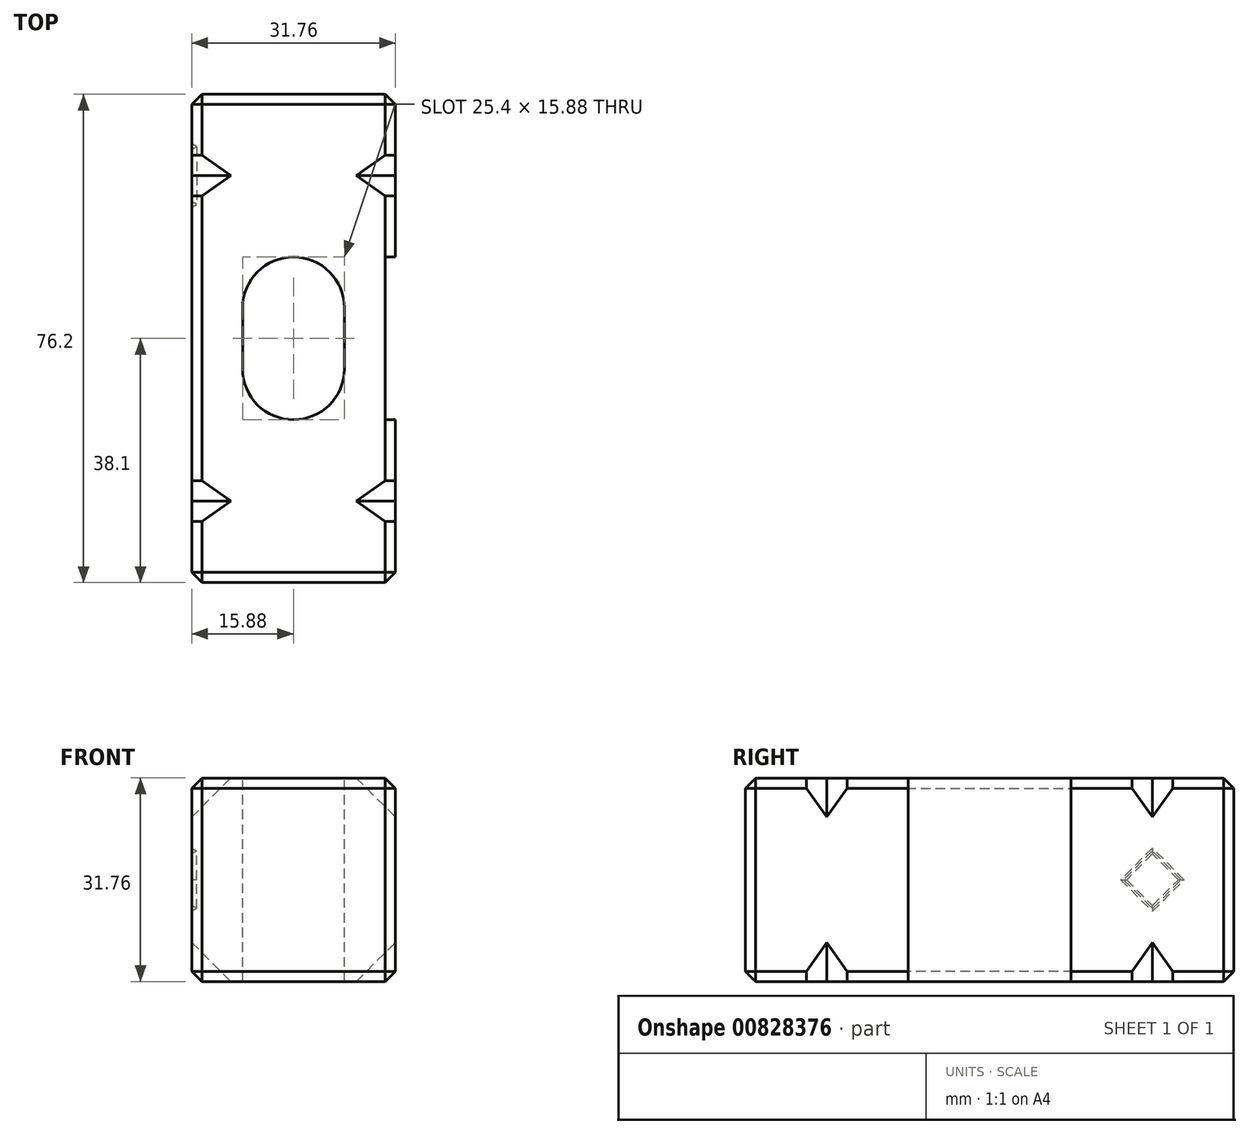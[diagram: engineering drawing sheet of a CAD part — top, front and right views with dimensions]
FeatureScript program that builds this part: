
annotation { "Feature Type Name" : "Feature", "Feature Type Description" : "" }
export const myFeature = defineFeature(function(context is Context, id is Id, definition is map)
    precondition{}
    {
        {
            var Q0;
            Q0=qCreatedBy(makeId("Front.planeOp"),FACE);
            var sketch = newSketch(context, id + "F0", { "sketchPlane" : qUnion([Q0])});
            skLineSegment(sketch, "E0", {"start": v(0, 15.88) * mm, "end": v(0, -15.88) * mm, "construction": true});
            skLineSegment(sketch, "E1", {"start": v(0, -15.88) * mm, "end": v(-15.87, 0) * mm, "construction": true});
            skLineSegment(sketch, "E2", {"start": v(-15.87, 0) * mm, "end": v(15.88, 0) * mm, "construction": true});
            skLineSegment(sketch, "E3.bottom", {"start": v(15.88, -15.88) * mm, "end": v(-15.87, -15.88) * mm});
            skLineSegment(sketch, "E3.top", {"start": v(15.88, 15.88) * mm, "end": v(-15.87, 15.88) * mm});
            skLineSegment(sketch, "E3.left", {"start": v(15.88, -15.88) * mm, "end": v(15.88, 15.88) * mm});
            skLineSegment(sketch, "E3.right", {"start": v(-15.87, -15.88) * mm, "end": v(-15.87, 15.88) * mm});
            skSolve(sketch);
        }
        {
            var Q0;
            Q0=makeQuery(id+"F0.imprint","IMPRINT",FACE,{"disambiguationData":[TD([[makeQuery(id+"F0.imprint","IMPRINT",EDGE,{"derivedFrom":sQuery(id+"F0.wireOp",EDGE,"E3.bottom")}),-1.0]])]});
            extrude(context, id + "F1", {"entities" : qUnion([Q0]), "endBound" : BoundingType.SYMMETRIC, "depth" : 76.2 * mm, "offsetDistance" : 25 * mm});
        }
        {
            var Q0;
            Q0=makeQuery(id+"F1.opExtrude","CAP_EDGE",EDGE,{"disambiguationData":[OSD([sQuery(id+"F0.wireOp",EDGE,"E3.top")])],"isStart":false});
            var Q1;
            Q1=makeQuery(id+"F1.opExtrude","CAP_EDGE",EDGE,{"disambiguationData":[OSD([sQuery(id+"F0.wireOp",EDGE,"E3.left")])],"isStart":false});
            var Q2;
            Q2=makeQuery(id+"F1.opExtrude","SWEPT_EDGE",EDGE,{"disambiguationData":[OSD([sQuery(id+"F0.wireOp",EDGE,"E3.top"),sQuery(id+"F0.wireOp",EDGE,"E3.left")])]});
            var Q3;
            Q3=makeQuery(id+"F1.opExtrude","SWEPT_EDGE",EDGE,{"disambiguationData":[OSD([sQuery(id+"F0.wireOp",EDGE,"E3.bottom"),sQuery(id+"F0.wireOp",EDGE,"E3.left")])]});
            var Q4;
            Q4=makeQuery(id+"F1.opExtrude","SWEPT_EDGE",EDGE,{"disambiguationData":[OSD([sQuery(id+"F0.wireOp",EDGE,"E3.top"),sQuery(id+"F0.wireOp",EDGE,"E3.right")])]});
            var Q5;
            Q5=makeQuery(id+"F1.opExtrude","CAP_EDGE",EDGE,{"disambiguationData":[OSD([sQuery(id+"F0.wireOp",EDGE,"E3.right")])],"isStart":false});
            var Q6;
            Q6=makeQuery(id+"F1.opExtrude","CAP_EDGE",EDGE,{"disambiguationData":[OSD([sQuery(id+"F0.wireOp",EDGE,"E3.bottom")])],"isStart":false});
            var Q7;
            Q7=makeQuery(id+"F1.opExtrude","CAP_EDGE",EDGE,{"disambiguationData":[OSD([sQuery(id+"F0.wireOp",EDGE,"E3.left")])],"isStart":true});
            var Q8;
            Q8=makeQuery(id+"F1.opExtrude","CAP_EDGE",EDGE,{"disambiguationData":[OSD([sQuery(id+"F0.wireOp",EDGE,"E3.right")])],"isStart":true});
            var Q9;
            Q9=makeQuery(id+"F1.opExtrude","CAP_EDGE",EDGE,{"disambiguationData":[OSD([sQuery(id+"F0.wireOp",EDGE,"E3.bottom")])],"isStart":true});
            var Q10;
            Q10=makeQuery(id+"F1.opExtrude","SWEPT_EDGE",EDGE,{"disambiguationData":[OSD([sQuery(id+"F0.wireOp",EDGE,"E3.bottom"),sQuery(id+"F0.wireOp",EDGE,"E3.right")])]});
            var Q11;
            Q11=makeQuery(id+"F1.opExtrude","CAP_EDGE",EDGE,{"disambiguationData":[OSD([sQuery(id+"F0.wireOp",EDGE,"E3.top")])],"isStart":true});
            chamfer(context, id + "F2", {"entities" : qUnion([Q0, Q1, Q2, Q3, Q4, Q5, Q6, Q7, Q8, Q9, Q10, Q11]), "width" : 1.59 * mm, "tangentPropagation" : true});
        }
        {
            var Q0;
            Q0=makeQuery(id+"F1.opExtrude","SWEPT_FACE",FACE,{"disambiguationData":[OSD([sQuery(id+"F0.wireOp",EDGE,"E3.top")])]});
            var sketch = newSketch(context, id + "F3", { "sketchPlane" : qUnion([Q0])});
            skLineSegment(sketch, "E4.0.0", {"start": v(14.29, -36.51) * mm, "end": v(14.29, 36.51) * mm});
            skLineSegment(sketch, "E4.0.1", {"start": v(14.29, 36.51) * mm, "end": v(-14.29, 36.51) * mm});
            skLineSegment(sketch, "E4.0.2", {"start": v(-14.29, 36.51) * mm, "end": v(-14.29, -36.51) * mm});
            skLineSegment(sketch, "E4.0.3", {"start": v(-14.29, -36.51) * mm, "end": v(14.29, -36.51) * mm});
            skLineSegment(sketch, "E5.0.0", {"start": v(-15.87, -36.51) * mm, "end": v(-14.29, -36.51) * mm});
            skLineSegment(sketch, "E5.0.1", {"start": v(-14.29, -36.51) * mm, "end": v(-14.29, 36.51) * mm});
            skLineSegment(sketch, "E5.0.2", {"start": v(-14.29, 36.51) * mm, "end": v(-15.87, 36.51) * mm});
            skLineSegment(sketch, "E5.0.3", {"start": v(-15.87, 36.51) * mm, "end": v(-15.87, -36.51) * mm});
            skLineSegment(sketch, "E6.0.0", {"start": v(14.29, -36.51) * mm, "end": v(15.88, -36.51) * mm});
            skLineSegment(sketch, "E6.0.1", {"start": v(15.88, -36.51) * mm, "end": v(15.88, 36.51) * mm});
            skLineSegment(sketch, "E6.0.2", {"start": v(14.29, 36.51) * mm, "end": v(15.88, 36.51) * mm});
            skLineSegment(sketch, "E6.0.3", {"start": v(14.29, 36.51) * mm, "end": v(14.29, -36.51) * mm});
            skLineSegment(sketch, "E7", {"start": v(-15.87, 0) * mm, "end": v(15.88, 0) * mm, "construction": true});
            skLineSegment(sketch, "E8", {"start": v(15.87, 12.7) * mm, "end": v(-15.87, 12.7) * mm, "construction": true});
            skLineSegment(sketch, "E9", {"start": v(-15.87, -12.7) * mm, "end": v(15.88, -12.7) * mm, "construction": true});
            skLineSegment(sketch, "E10", {"start": v(11.11, 36.51) * mm, "end": v(11.11, -36.51) * mm, "construction": true});
            skLineSegment(sketch, "E11", {"start": v(-11.11, 36.51) * mm, "end": v(-11.11, -36.51) * mm, "construction": true});
            skLineSegment(sketch, "E12", {"start": v(0, 36.51) * mm, "end": v(0, -36.51) * mm, "construction": true});
            skLineSegment(sketch, "E13", {"start": v(-14.29, 36.51) * mm, "end": v(-14.29, -36.51) * mm, "construction": true});
            skArc(sketch, "E14", {"start": v(-11.11, 12.7) * mm, "mid": v(-14.29, 0) * mm, "end": v(-11.11, -12.7) * mm});
            skLineSegment(sketch, "E15", {"start": v(-11.11, 12.7) * mm, "end": v(-15.87, 12.7) * mm});
            skLineSegment(sketch, "E16", {"start": v(-11.11, -12.7) * mm, "end": v(-15.87, -12.7) * mm});
            skLineSegment(sketch, "E17.MirrorCS", {"start": v(11.11, 12.7) * mm, "end": v(15.88, 12.7) * mm});
            skArc(sketch, "E18.MirrorCS", {"start": v(11.11, 12.7) * mm, "mid": v(14.29, 0) * mm, "end": v(11.11, -12.7) * mm});
            skLineSegment(sketch, "E19.MirrorCS", {"start": v(11.11, -12.7) * mm, "end": v(15.88, -12.7) * mm});
            skArc(sketch, "E20", {"start": v(-7.94, -4.76) * mm, "mid": v(0, -12.7) * mm, "end": v(7.94, -4.76) * mm});
            skLineSegment(sketch, "E21", {"start": v(7.94, 4.76) * mm, "end": v(7.94, -4.76) * mm});
            skLineSegment(sketch, "E22", {"start": v(-7.94, 4.76) * mm, "end": v(-7.94, -4.76) * mm});
            skArc(sketch, "E23.trimOffspring", {"start": v(7.94, 4.76) * mm, "mid": v(0, 12.7) * mm, "end": v(-7.94, 4.76) * mm});
            skSolve(sketch);
        }
        {
            var Q0;
            {var subQ0=sQuery(id+"F3.wireOp",EDGE,"E15");var subQ1=sQuery(id+"F3.wireOp",EDGE,"E5.0.1");var subQ2=makeQuery(id+"F3.imprint","INTERSECT",VERTEX,{"derivedFrom":[subQ1,subQ0]});Q0=makeQuery(id+"F3.imprint","IMPRINT",FACE,{"disambiguationData":[TD([[makeQuery(id+"F3.imprint","IMPRINT",EDGE,{"disambiguationData":[TD([[subQ2,-1.0]])],"derivedFrom":subQ1}),1.0]])]});}
            var Q1;
            {var subQ1=sQuery(id+"F3.wireOp",EDGE,"E5.0.1");var subQ4=sQuery(id+"F3.wireOp",EDGE,"E15");var subQ10=makeQuery(id+"F3.imprint","INTERSECT",VERTEX,{"derivedFrom":[subQ1,subQ4]});Q1=makeQuery(id+"F3.imprint","IMPRINT",FACE,{"disambiguationData":[TD([[makeQuery(id+"F3.imprint","IMPRINT",EDGE,{"disambiguationData":[TD([[subQ10,-1.0]])],"derivedFrom":subQ1}),-1.0]])]});}
            var Q2;
            {var subQ0=sQuery(id+"F3.wireOp",EDGE,"E14");var subQ1=sQuery(id+"F3.wireOp",EDGE,"E5.0.1");var subQ2=makeQuery(id+"F3.imprint","INTERSECT",VERTEX,{"disambiguationData":[OD(1.0)],"derivedFrom":[subQ1,subQ0]});Q2=makeQuery(id+"F3.imprint","IMPRINT",FACE,{"disambiguationData":[TD([[makeQuery(id+"F3.imprint","IMPRINT",EDGE,{"disambiguationData":[TD([[subQ2,-1.0]])],"derivedFrom":subQ1}),1.0]])]});}
            var Q3;
            {var subQ0=sQuery(id+"F3.wireOp",EDGE,"E19.MirrorCS");var subQ1=sQuery(id+"F3.wireOp",EDGE,"E6.0.3");var subQ2=makeQuery(id+"F3.imprint","INTERSECT",VERTEX,{"derivedFrom":[subQ1,subQ0]});Q3=makeQuery(id+"F3.imprint","IMPRINT",FACE,{"disambiguationData":[TD([[makeQuery(id+"F3.imprint","IMPRINT",EDGE,{"disambiguationData":[TD([[subQ2,-1.0]])],"derivedFrom":subQ1}),1.0]])]});}
            var Q4;
            {var subQ0=sQuery(id+"F3.wireOp",EDGE,"E17.MirrorCS");var subQ1=sQuery(id+"F3.wireOp",EDGE,"E6.0.1");var subQ2=makeQuery(id+"F3.imprint","INTERSECT",VERTEX,{"derivedFrom":[subQ1,subQ0]});Q4=makeQuery(id+"F3.imprint","IMPRINT",FACE,{"disambiguationData":[TD([[makeQuery(id+"F3.imprint","IMPRINT",EDGE,{"disambiguationData":[TD([[subQ2,1.0]])],"derivedFrom":subQ1}),1.0]])]});}
            var Q5;
            {var subQ0=sQuery(id+"F3.wireOp",EDGE,"E18.MirrorCS");var subQ1=sQuery(id+"F3.wireOp",EDGE,"E6.0.3");var subQ2=makeQuery(id+"F3.imprint","INTERSECT",VERTEX,{"disambiguationData":[OD(1.0)],"derivedFrom":[subQ1,subQ0]});Q5=makeQuery(id+"F3.imprint","IMPRINT",FACE,{"disambiguationData":[TD([[makeQuery(id+"F3.imprint","IMPRINT",EDGE,{"disambiguationData":[TD([[subQ2,-1.0]])],"derivedFrom":subQ1}),1.0]])]});}
            var Q6;
            Q6=makeQuery(id+"F3.imprint","IMPRINT",FACE,{"disambiguationData":[TD([[makeQuery(id+"F3.imprint","IMPRINT",EDGE,{"derivedFrom":sQuery(id+"F3.wireOp",EDGE,"E20")}),1.0]])]});
            extrude(context, id + "F4", {"entities" : qUnion([Q0, Q1, Q2, Q3, Q4, Q5, Q6]), "operationType" : NewBodyOperationType.REMOVE, "endBound" : BoundingType.THROUGH_ALL, "oppositeDirection" : true, "depth" : 25.4 * mm, "offsetDistance" : 25.4 * mm});
        }
        {
            var Q0;
            {var subQ0=sQuery(id+"F0.wireOp",EDGE,"E3.right");var subQ1=sQuery(id+"F0.wireOp",EDGE,"E3.top");Q0=makeQuery(id+"F2.opChamfer","BLEND_VERTEX",VERTEX,{"blendedFrom":[makeQuery(id+"F1.opExtrude","CAP_VERTEX",VERTEX,{"disambiguationData":[OSD([subQ1,subQ0])],"isStart":true}),makeQuery(id+"F1.opExtrude","CAP_EDGE",EDGE,{"disambiguationData":[OSD([subQ1])],"isStart":true}),makeQuery(id+"F1.opExtrude","CAP_EDGE",EDGE,{"disambiguationData":[OSD([subQ0])],"isStart":true}),makeQuery(id+"F1.opExtrude","CAP_FACE",FACE,{"disambiguationData":[OSD([sQuery(id+"F0.wireOp",EDGE,"E3.bottom"),subQ1,sQuery(id+"F0.wireOp",EDGE,"E3.left"),subQ0])],"isStart":true})],"blendedInto":[makeQuery(id+"F1.opExtrude","CAP_FACE",FACE,{"disambiguationData":[OSD([sQuery(id+"F0.wireOp",EDGE,"E3.bottom"),subQ1,sQuery(id+"F0.wireOp",EDGE,"E3.left"),subQ0])],"isStart":true})]});}
            var Q1;
            {var subQ0=sQuery(id+"F0.wireOp",EDGE,"E3.left");var subQ1=sQuery(id+"F0.wireOp",EDGE,"E3.bottom");Q1=makeQuery(id+"F2.opChamfer","BLEND_VERTEX",VERTEX,{"blendedFrom":[makeQuery(id+"F1.opExtrude","CAP_VERTEX",VERTEX,{"disambiguationData":[OSD([subQ1,subQ0])],"isStart":true}),makeQuery(id+"F1.opExtrude","CAP_EDGE",EDGE,{"disambiguationData":[OSD([subQ1])],"isStart":true}),makeQuery(id+"F1.opExtrude","CAP_EDGE",EDGE,{"disambiguationData":[OSD([subQ0])],"isStart":true}),makeQuery(id+"F1.opExtrude","CAP_FACE",FACE,{"disambiguationData":[OSD([subQ1,sQuery(id+"F0.wireOp",EDGE,"E3.top"),subQ0,sQuery(id+"F0.wireOp",EDGE,"E3.right")])],"isStart":true})],"blendedInto":[makeQuery(id+"F1.opExtrude","CAP_FACE",FACE,{"disambiguationData":[OSD([subQ1,sQuery(id+"F0.wireOp",EDGE,"E3.top"),subQ0,sQuery(id+"F0.wireOp",EDGE,"E3.right")])],"isStart":true})]});}
            var Q2;
            {var subQ0=sQuery(id+"F0.wireOp",EDGE,"E3.left");var subQ1=sQuery(id+"F0.wireOp",EDGE,"E3.bottom");Q2=makeQuery(id+"F2.opChamfer","BLEND_VERTEX",VERTEX,{"blendedFrom":[makeQuery(id+"F1.opExtrude","CAP_VERTEX",VERTEX,{"disambiguationData":[OSD([subQ1,subQ0])],"isStart":false}),makeQuery(id+"F1.opExtrude","CAP_EDGE",EDGE,{"disambiguationData":[OSD([subQ1])],"isStart":false}),makeQuery(id+"F1.opExtrude","CAP_EDGE",EDGE,{"disambiguationData":[OSD([subQ0])],"isStart":false}),makeQuery(id+"F1.opExtrude","CAP_FACE",FACE,{"disambiguationData":[OSD([subQ1,sQuery(id+"F0.wireOp",EDGE,"E3.top"),subQ0,sQuery(id+"F0.wireOp",EDGE,"E3.right")])],"isStart":false})],"blendedInto":[makeQuery(id+"F1.opExtrude","CAP_FACE",FACE,{"disambiguationData":[OSD([subQ1,sQuery(id+"F0.wireOp",EDGE,"E3.top"),subQ0,sQuery(id+"F0.wireOp",EDGE,"E3.right")])],"isStart":false})]});}
            cPlane(context, id + "F5", {"entities" : qUnion([Q0, Q1, Q2]), "cplaneType" : CPlaneType.THREE_POINT, "offset" : 25.4 * mm, "width" : 152.4 * mm, "height" : 152.4 * mm});
        }
        {
            var Q0;
            Q0=qCreatedBy(id+"F5.planeOp",FACE);
            var sketch = newSketch(context, id + "F6", { "sketchPlane" : qUnion([Q0])});
            skEllipticalArc(sketch, "E24.0.0", {});
            skLineSegment(sketch, "E24.0.1", {"start": v(-12.7, 19.08) * mm, "end": v(-12.7, 21.33) * mm});
            skLineSegment(sketch, "E24.0.2", {"start": v(-12.7, 21.33) * mm, "end": v(-36.51, 21.33) * mm});
            skLineSegment(sketch, "E24.0.3", {"start": v(-36.51, 21.33) * mm, "end": v(-36.51, 1.12) * mm});
            skLineSegment(sketch, "E24.0.4", {"start": v(-36.51, 1.12) * mm, "end": v(-12.7, 1.12) * mm});
            skLineSegment(sketch, "E24.0.5", {"start": v(-12.7, 1.12) * mm, "end": v(-12.7, 3.37) * mm});
            skEllipticalArc(sketch, "E24.0.6", {});
            skLineSegment(sketch, "E24.0.7", {"start": v(12.7, 3.37) * mm, "end": v(12.7, 1.12) * mm});
            skLineSegment(sketch, "E24.0.8", {"start": v(12.7, 1.12) * mm, "end": v(36.51, 1.12) * mm});
            skLineSegment(sketch, "E24.0.9", {"start": v(36.51, 1.12) * mm, "end": v(36.51, 21.33) * mm});
            skLineSegment(sketch, "E24.0.10", {"start": v(36.51, 21.33) * mm, "end": v(12.7, 21.33) * mm});
            skLineSegment(sketch, "E24.0.11", {"start": v(12.7, 21.33) * mm, "end": v(12.7, 19.08) * mm});
            skLineSegment(sketch, "E25.0.0", {"start": v(-38.1, 20.2) * mm, "end": v(-38.1, 0) * mm});
            skLineSegment(sketch, "E25.0.1", {"start": v(-38.1, 0) * mm, "end": v(-38.1, -20.2) * mm});
            skLineSegment(sketch, "E25.0.2", {"start": v(-38.1, -20.2) * mm, "end": v(-38.1, 0) * mm});
            skLineSegment(sketch, "E25.0.3", {"start": v(-38.1, 0) * mm, "end": v(-38.1, 20.2) * mm});
            skLineSegment(sketch, "E26.0.0", {"start": v(-36.51, -21.33) * mm, "end": v(-12.7, -21.33) * mm});
            skLineSegment(sketch, "E26.0.1", {"start": v(-12.7, -21.33) * mm, "end": v(-12.7, -1.12) * mm});
            skLineSegment(sketch, "E26.0.2", {"start": v(-12.7, -1.12) * mm, "end": v(-36.51, -1.12) * mm});
            skLineSegment(sketch, "E26.0.3", {"start": v(-36.51, -1.12) * mm, "end": v(-36.51, -21.33) * mm});
            skLineSegment(sketch, "E27.0.0", {"start": v(12.7, -1.12) * mm, "end": v(12.7, -21.33) * mm});
            skLineSegment(sketch, "E27.0.1", {"start": v(12.7, -21.33) * mm, "end": v(36.51, -21.33) * mm});
            skLineSegment(sketch, "E27.0.2", {"start": v(36.51, -21.33) * mm, "end": v(36.51, -1.12) * mm});
            skLineSegment(sketch, "E27.0.3", {"start": v(36.51, -1.12) * mm, "end": v(12.7, -1.12) * mm});
            skLineSegment(sketch, "E28.0.0", {"start": v(36.51, 1.12) * mm, "end": v(12.7, 1.12) * mm});
            skLineSegment(sketch, "E28.0.1", {"start": v(12.7, 1.12) * mm, "end": v(12.7, -1.12) * mm});
            skLineSegment(sketch, "E28.0.2", {"start": v(12.7, -1.12) * mm, "end": v(36.51, -1.12) * mm});
            skLineSegment(sketch, "E28.0.3", {"start": v(36.51, 1.12) * mm, "end": v(36.51, -1.12) * mm});
            skLineSegment(sketch, "E29.0.0", {"start": v(-12.7, 1.12) * mm, "end": v(-12.7, -1.12) * mm});
            skLineSegment(sketch, "E29.0.1", {"start": v(-12.7, 1.12) * mm, "end": v(-36.51, 1.12) * mm});
            skLineSegment(sketch, "E29.0.2", {"start": v(-36.51, 1.12) * mm, "end": v(-36.51, -1.12) * mm});
            skLineSegment(sketch, "E29.0.3", {"start": v(-36.51, -1.12) * mm, "end": v(-12.7, -1.12) * mm});
            skEllipticalArc(sketch, "E30.0.0", {});
            skLineSegment(sketch, "E30.0.1", {"start": v(12.7, -19.08) * mm, "end": v(12.7, 3.37) * mm});
            skEllipticalArc(sketch, "E30.0.2", {});
            skLineSegment(sketch, "E30.0.3", {"start": v(-12.7, 3.37) * mm, "end": v(-12.7, -19.08) * mm});
            skLineSegment(sketch, "E31.0.1", {"start": v(-12.7, -21.33) * mm, "end": v(-36.51, -21.33) * mm});
            skLineSegment(sketch, "E32.0.0", {"start": v(36.51, -21.33) * mm, "end": v(12.7, -21.33) * mm});
            skLineSegment(sketch, "E33.0.1", {"start": v(-12.7, -1.12) * mm, "end": v(-12.7, -3.37) * mm});
            skEllipticalArc(sketch, "E33.0.2", {});
            skLineSegment(sketch, "E33.0.3", {"start": v(12.7, -3.37) * mm, "end": v(12.7, -1.12) * mm});
            skLineSegment(sketch, "E33.0.5", {"start": v(36.51, -1.12) * mm, "end": v(36.51, -21.33) * mm});
            skLineSegment(sketch, "E33.0.7", {"start": v(12.7, -21.33) * mm, "end": v(12.7, -19.08) * mm});
            skEllipticalArc(sketch, "E33.0.8", {});
            skLineSegment(sketch, "E33.0.9", {"start": v(-12.7, -19.08) * mm, "end": v(-12.7, -21.33) * mm});
            skLineSegment(sketch, "E33.0.11", {"start": v(-36.51, -21.33) * mm, "end": v(-36.51, -1.12) * mm});
            skLineSegment(sketch, "E34.0.0", {"start": v(38.1, -20.2) * mm, "end": v(38.1, 0) * mm});
            skLineSegment(sketch, "E34.0.1", {"start": v(38.1, 0) * mm, "end": v(38.1, 20.2) * mm});
            skLineSegment(sketch, "E34.0.2", {"start": v(38.1, 20.2) * mm, "end": v(38.1, 0) * mm});
            skLineSegment(sketch, "E34.0.3", {"start": v(38.1, 0) * mm, "end": v(38.1, -20.2) * mm});
            skLineSegment(sketch, "E35", {"start": v(-25.4, 21.33) * mm, "end": v(-25.4, -21.33) * mm, "construction": true});
            skLineSegment(sketch, "E36", {"start": v(25.4, -21.33) * mm, "end": v(25.4, 21.33) * mm, "construction": true});
            skLineSegment(sketch, "E37", {"start": v(0, 38.1) * mm, "end": v(0, -38.1) * mm, "construction": true});
            skLineSegment(sketch, "E38", {"start": v(-25.4, 18.15) * mm, "end": v(-22.22, 21.33) * mm});
            skLineSegment(sketch, "E39", {"start": v(-22.22, 21.33) * mm, "end": v(-25.4, 18.15) * mm});
            skLineSegment(sketch, "E40", {"start": v(-25.4, 18.15) * mm, "end": v(-28.58, 21.33) * mm});
            skLineSegment(sketch, "E41", {"start": v(-38.1, 0) * mm, "end": v(38.1, 0) * mm, "construction": true});
            skLineSegment(sketch, "E42.MirrorCS", {"start": v(-25.4, -18.15) * mm, "end": v(-22.22, -21.33) * mm});
            skLineSegment(sketch, "E43.MirrorCS", {"start": v(-25.4, -18.15) * mm, "end": v(-28.58, -21.33) * mm});
            skLineSegment(sketch, "E44.MirrorCS", {"start": v(25.4, 18.15) * mm, "end": v(22.22, 21.33) * mm});
            skLineSegment(sketch, "E45.MirrorCS", {"start": v(25.4, 18.15) * mm, "end": v(28.58, 21.33) * mm});
            skLineSegment(sketch, "E46.MirrorCS", {"start": v(25.4, -18.15) * mm, "end": v(22.22, -21.33) * mm});
            skLineSegment(sketch, "E47.MirrorCS", {"start": v(25.4, -18.15) * mm, "end": v(28.58, -21.33) * mm});
            const initialGuessF6  = {"E24.0.0": [0, 0.002245064030267274, 1, 0, 0.02698750000000002, 0.01908304425727196, 1.0808390005411692, 2.060753653048625], "E24.0.6": [0, 0.020205576272405608, 1, 0, 0.02698750000000002, 0.01908304425727196, 4.222431654130961, 5.202346306638417], "E30.0.0": [0, -0.00224506403026728, 1, 0, 0.02698750000000002, 0.019083044257271958, 4.222431654130962, 5.202346306638416], "E30.0.2": [0, 0.020205576272405608, -1, 0, 0.02698750000000002, 0.01908304425727196, 1.0808390005411683, 2.0607536530486246], "E33.0.2": [0, -0.020205576272405615, -1, 0, 0.02698750000000002, 0.019083044257271958, 4.222431654130962, 5.202346306638418], "E33.0.8": [0, -0.00224506403026728, -1, 0, 0.02698750000000002, 0.019083044257271958, 1.0808390005411688, 2.0607536530486237]};
            skSetInitialGuess(sketch, initialGuessF6);
            skSolve(sketch);
        }
        {
            var Q0;
            {var subQ2=sQuery(id+"F6.wireOp",EDGE,"E38");Q0=makeQuery(id+"F6.imprint","IMPRINT",FACE,{"disambiguationData":[TD([[makeQuery(id+"F6.imprint","IMPRINT",EDGE,{"derivedFrom":subQ2}),1.0]])]});}
            var Q1;
            {var subQ0=sQuery(id+"F6.wireOp",EDGE,"E42.MirrorCS");Q1=makeQuery(id+"F6.imprint","IMPRINT",FACE,{"disambiguationData":[TD([[makeQuery(id+"F6.imprint","IMPRINT",EDGE,{"derivedFrom":subQ0}),-1.0]])]});}
            var Q2;
            {var subQ2=sQuery(id+"F6.wireOp",EDGE,"E46.MirrorCS");Q2=makeQuery(id+"F6.imprint","IMPRINT",FACE,{"disambiguationData":[TD([[makeQuery(id+"F6.imprint","IMPRINT",EDGE,{"derivedFrom":subQ2}),1.0]])]});}
            var Q3;
            {var subQ0=sQuery(id+"F6.wireOp",EDGE,"E44.MirrorCS");Q3=makeQuery(id+"F6.imprint","IMPRINT",FACE,{"disambiguationData":[TD([[makeQuery(id+"F6.imprint","IMPRINT",EDGE,{"derivedFrom":subQ0}),-1.0]])]});}
            extrude(context, id + "F7", {"entities" : qUnion([Q0, Q1, Q2, Q3]), "operationType" : NewBodyOperationType.REMOVE, "endBound" : BoundingType.SYMMETRIC, "oppositeDirection" : true, "depth" : 25.4 * mm, "offsetDistance" : 25.4 * mm});
        }
        {
            var Q0;
            {var subQ0=sQuery(id+"F0.wireOp",EDGE,"E3.left");var subQ1=sQuery(id+"F0.wireOp",EDGE,"E3.top");Q0=makeQuery(id+"F2.opChamfer","BLEND_VERTEX",VERTEX,{"blendedFrom":[makeQuery(id+"F1.opExtrude","CAP_VERTEX",VERTEX,{"disambiguationData":[OSD([subQ1,subQ0])],"isStart":true}),makeQuery(id+"F1.opExtrude","CAP_EDGE",EDGE,{"disambiguationData":[OSD([subQ1])],"isStart":true}),makeQuery(id+"F1.opExtrude","CAP_EDGE",EDGE,{"disambiguationData":[OSD([subQ0])],"isStart":true}),makeQuery(id+"F1.opExtrude","CAP_FACE",FACE,{"disambiguationData":[OSD([sQuery(id+"F0.wireOp",EDGE,"E3.bottom"),subQ1,subQ0,sQuery(id+"F0.wireOp",EDGE,"E3.right")])],"isStart":true})],"blendedInto":[makeQuery(id+"F1.opExtrude","CAP_FACE",FACE,{"disambiguationData":[OSD([sQuery(id+"F0.wireOp",EDGE,"E3.bottom"),subQ1,subQ0,sQuery(id+"F0.wireOp",EDGE,"E3.right")])],"isStart":true})]});}
            var Q1;
            {var subQ0=sQuery(id+"F0.wireOp",EDGE,"E3.right");var subQ1=sQuery(id+"F0.wireOp",EDGE,"E3.bottom");Q1=makeQuery(id+"F2.opChamfer","BLEND_VERTEX",VERTEX,{"blendedFrom":[makeQuery(id+"F1.opExtrude","CAP_VERTEX",VERTEX,{"disambiguationData":[OSD([subQ1,subQ0])],"isStart":true}),makeQuery(id+"F1.opExtrude","CAP_EDGE",EDGE,{"disambiguationData":[OSD([subQ1])],"isStart":true}),makeQuery(id+"F1.opExtrude","CAP_EDGE",EDGE,{"disambiguationData":[OSD([subQ0])],"isStart":true}),makeQuery(id+"F1.opExtrude","CAP_FACE",FACE,{"disambiguationData":[OSD([subQ1,sQuery(id+"F0.wireOp",EDGE,"E3.top"),sQuery(id+"F0.wireOp",EDGE,"E3.left"),subQ0])],"isStart":true})],"blendedInto":[makeQuery(id+"F1.opExtrude","CAP_FACE",FACE,{"disambiguationData":[OSD([subQ1,sQuery(id+"F0.wireOp",EDGE,"E3.top"),sQuery(id+"F0.wireOp",EDGE,"E3.left"),subQ0])],"isStart":true})]});}
            var Q2;
            {var subQ0=sQuery(id+"F0.wireOp",EDGE,"E3.left");var subQ1=sQuery(id+"F0.wireOp",EDGE,"E3.top");Q2=makeQuery(id+"F2.opChamfer","BLEND_VERTEX",VERTEX,{"blendedFrom":[makeQuery(id+"F1.opExtrude","CAP_VERTEX",VERTEX,{"disambiguationData":[OSD([subQ1,subQ0])],"isStart":false}),makeQuery(id+"F1.opExtrude","CAP_EDGE",EDGE,{"disambiguationData":[OSD([subQ1])],"isStart":false}),makeQuery(id+"F1.opExtrude","CAP_EDGE",EDGE,{"disambiguationData":[OSD([subQ0])],"isStart":false}),makeQuery(id+"F1.opExtrude","CAP_FACE",FACE,{"disambiguationData":[OSD([sQuery(id+"F0.wireOp",EDGE,"E3.bottom"),subQ1,subQ0,sQuery(id+"F0.wireOp",EDGE,"E3.right")])],"isStart":false})],"blendedInto":[makeQuery(id+"F1.opExtrude","CAP_FACE",FACE,{"disambiguationData":[OSD([sQuery(id+"F0.wireOp",EDGE,"E3.bottom"),subQ1,subQ0,sQuery(id+"F0.wireOp",EDGE,"E3.right")])],"isStart":false})]});}
            cPlane(context, id + "F8", {"entities" : qUnion([Q0, Q1, Q2]), "cplaneType" : CPlaneType.THREE_POINT, "offset" : 25.4 * mm, "width" : 152.4 * mm, "height" : 152.4 * mm});
        }
        {
            var Q0;
            Q0=qCreatedBy(id+"F8.planeOp",FACE);
            var sketch = newSketch(context, id + "F9", { "sketchPlane" : qUnion([Q0])});
            skLineSegment(sketch, "E48.0.0", {"start": v(12.7, -1.12) * mm, "end": v(22.22, -1.12) * mm});
            skLineSegment(sketch, "E48.0.1", {"start": v(22.23, -1.12) * mm, "end": v(25.4, -4.3) * mm});
            skLineSegment(sketch, "E48.0.2", {"start": v(25.4, -4.3) * mm, "end": v(28.57, -1.12) * mm});
            skLineSegment(sketch, "E48.0.3", {"start": v(28.57, -1.12) * mm, "end": v(36.51, -1.12) * mm});
            skLineSegment(sketch, "E48.0.4", {"start": v(36.51, -1.12) * mm, "end": v(36.51, -21.33) * mm});
            skLineSegment(sketch, "E48.0.5", {"start": v(36.51, -21.33) * mm, "end": v(12.7, -21.33) * mm});
            skLineSegment(sketch, "E48.0.6", {"start": v(12.7, -21.33) * mm, "end": v(12.7, -1.12) * mm});
            skLineSegment(sketch, "E49.0.0", {"start": v(-28.58, -1.12) * mm, "end": v(-25.4, -4.3) * mm});
            skLineSegment(sketch, "E49.0.1", {"start": v(-25.4, -4.3) * mm, "end": v(-22.23, -1.12) * mm});
            skLineSegment(sketch, "E49.0.2", {"start": v(-22.23, -1.12) * mm, "end": v(-12.7, -1.12) * mm});
            skLineSegment(sketch, "E49.0.3", {"start": v(-12.7, -1.12) * mm, "end": v(-12.7, -21.33) * mm});
            skLineSegment(sketch, "E49.0.4", {"start": v(-12.7, -21.33) * mm, "end": v(-36.51, -21.33) * mm});
            skLineSegment(sketch, "E49.0.5", {"start": v(-36.51, -21.33) * mm, "end": v(-36.51, -1.12) * mm});
            skLineSegment(sketch, "E49.0.6", {"start": v(-36.51, -1.12) * mm, "end": v(-28.58, -1.12) * mm});
            skLineSegment(sketch, "E50.0.1", {"start": v(-12.7, 21.33) * mm, "end": v(-36.51, 21.33) * mm});
            skLineSegment(sketch, "E50.0.3", {"start": v(-36.51, 21.33) * mm, "end": v(-12.7, 21.33) * mm});
            skLineSegment(sketch, "E51.0.0", {"start": v(36.51, 21.33) * mm, "end": v(12.7, 21.33) * mm});
            skLineSegment(sketch, "E51.0.2", {"start": v(12.7, 21.33) * mm, "end": v(36.51, 21.33) * mm});
            skLineSegment(sketch, "E52.0.0", {"start": v(-25.4, 4.3) * mm, "end": v(-22.22, 1.12) * mm});
            skLineSegment(sketch, "E52.0.1", {"start": v(-22.22, 1.12) * mm, "end": v(-12.7, 1.12) * mm});
            skLineSegment(sketch, "E52.0.2", {"start": v(-12.7, 1.12) * mm, "end": v(-12.7, 21.33) * mm});
            skLineSegment(sketch, "E52.0.4", {"start": v(-36.51, 21.33) * mm, "end": v(-36.51, 1.12) * mm});
            skLineSegment(sketch, "E52.0.5", {"start": v(-36.51, 1.12) * mm, "end": v(-28.58, 1.12) * mm});
            skLineSegment(sketch, "E52.0.6", {"start": v(-28.57, 1.12) * mm, "end": v(-25.4, 4.3) * mm});
            skLineSegment(sketch, "E53.0.0", {"start": v(25.4, 4.3) * mm, "end": v(28.58, 1.12) * mm});
            skLineSegment(sketch, "E53.0.1", {"start": v(28.58, 1.12) * mm, "end": v(36.51, 1.12) * mm});
            skLineSegment(sketch, "E53.0.2", {"start": v(36.51, 1.12) * mm, "end": v(36.51, 21.33) * mm});
            skLineSegment(sketch, "E53.0.4", {"start": v(12.7, 21.33) * mm, "end": v(12.7, 1.12) * mm});
            skLineSegment(sketch, "E53.0.5", {"start": v(12.7, 1.12) * mm, "end": v(22.22, 1.12) * mm});
            skLineSegment(sketch, "E53.0.6", {"start": v(22.23, 1.12) * mm, "end": v(25.4, 4.3) * mm});
            skLineSegment(sketch, "E54.0.0", {"start": v(36.51, -1.12) * mm, "end": v(28.58, -1.12) * mm});
            skLineSegment(sketch, "E54.0.1", {"start": v(28.58, -1.12) * mm, "end": v(25.4, -4.3) * mm});
            skLineSegment(sketch, "E54.0.2", {"start": v(25.4, -4.3) * mm, "end": v(22.23, -1.12) * mm});
            skLineSegment(sketch, "E54.0.3", {"start": v(22.23, -1.12) * mm, "end": v(12.7, -1.12) * mm});
            skLineSegment(sketch, "E54.0.4", {"start": v(12.7, -1.12) * mm, "end": v(12.7, -3.37) * mm});
            skEllipticalArc(sketch, "E54.0.5", {});
            skLineSegment(sketch, "E54.0.6", {"start": v(-12.7, -3.37) * mm, "end": v(-12.7, -1.12) * mm});
            skLineSegment(sketch, "E54.0.7", {"start": v(-12.7, -1.12) * mm, "end": v(-22.22, -1.12) * mm});
            skLineSegment(sketch, "E54.0.8", {"start": v(-22.22, -1.12) * mm, "end": v(-25.4, -4.3) * mm});
            skLineSegment(sketch, "E54.0.9", {"start": v(-25.4, -4.3) * mm, "end": v(-28.57, -1.12) * mm});
            skLineSegment(sketch, "E54.0.10", {"start": v(-28.57, -1.12) * mm, "end": v(-36.51, -1.12) * mm});
            skLineSegment(sketch, "E54.0.11", {"start": v(-36.51, -1.12) * mm, "end": v(-36.51, -21.33) * mm});
            skLineSegment(sketch, "E54.0.12", {"start": v(-36.51, -21.33) * mm, "end": v(-12.7, -21.33) * mm});
            skLineSegment(sketch, "E54.0.13", {"start": v(-12.7, -21.33) * mm, "end": v(-12.7, -19.08) * mm});
            skEllipticalArc(sketch, "E54.0.14", {});
            skLineSegment(sketch, "E54.0.15", {"start": v(12.7, -19.08) * mm, "end": v(12.7, -21.33) * mm});
            skLineSegment(sketch, "E54.0.16", {"start": v(12.7, -21.33) * mm, "end": v(36.51, -21.33) * mm});
            skLineSegment(sketch, "E54.0.17", {"start": v(36.51, -21.33) * mm, "end": v(36.51, -1.12) * mm});
            skLineSegment(sketch, "E55.0.0", {"start": v(25.4, 4.3) * mm, "end": v(22.23, 1.12) * mm});
            skLineSegment(sketch, "E55.0.1", {"start": v(22.23, 1.12) * mm, "end": v(12.7, 1.12) * mm});
            skLineSegment(sketch, "E55.0.2", {"start": v(12.7, 1.12) * mm, "end": v(12.7, 3.37) * mm});
            skEllipticalArc(sketch, "E55.0.3", {});
            skLineSegment(sketch, "E55.0.4", {"start": v(-12.7, 3.37) * mm, "end": v(-12.7, 1.12) * mm});
            skLineSegment(sketch, "E55.0.5", {"start": v(-12.7, 1.12) * mm, "end": v(-22.22, 1.12) * mm});
            skLineSegment(sketch, "E55.0.6", {"start": v(-22.23, 1.12) * mm, "end": v(-25.4, 4.3) * mm});
            skLineSegment(sketch, "E55.0.7", {"start": v(-25.4, 4.3) * mm, "end": v(-28.58, 1.12) * mm});
            skLineSegment(sketch, "E55.0.8", {"start": v(-28.58, 1.12) * mm, "end": v(-36.51, 1.12) * mm});
            skLineSegment(sketch, "E55.0.9", {"start": v(-36.51, 1.12) * mm, "end": v(-36.51, 21.33) * mm});
            skLineSegment(sketch, "E55.0.11", {"start": v(-12.7, 21.33) * mm, "end": v(-12.7, 19.08) * mm});
            skEllipticalArc(sketch, "E55.0.12", {});
            skLineSegment(sketch, "E55.0.13", {"start": v(12.7, 19.08) * mm, "end": v(12.7, 21.33) * mm});
            skLineSegment(sketch, "E55.0.15", {"start": v(36.51, 21.33) * mm, "end": v(36.51, 1.12) * mm});
            skLineSegment(sketch, "E55.0.16", {"start": v(36.51, 1.12) * mm, "end": v(28.58, 1.12) * mm});
            skLineSegment(sketch, "E55.0.17", {"start": v(28.57, 1.12) * mm, "end": v(25.4, 4.3) * mm});
            skLineSegment(sketch, "E56.0.0", {"start": v(38.1, 0) * mm, "end": v(38.1, -20.2) * mm});
            skLineSegment(sketch, "E56.0.1", {"start": v(38.1, -20.2) * mm, "end": v(38.1, 0) * mm});
            skLineSegment(sketch, "E56.0.2", {"start": v(38.1, 0) * mm, "end": v(38.1, 20.2) * mm});
            skLineSegment(sketch, "E56.0.3", {"start": v(38.1, 20.2) * mm, "end": v(38.1, 0) * mm});
            skLineSegment(sketch, "E57.0.0", {"start": v(-38.1, 0) * mm, "end": v(-38.1, -20.2) * mm});
            skLineSegment(sketch, "E57.0.1", {"start": v(-38.1, -20.2) * mm, "end": v(-38.1, 0) * mm});
            skLineSegment(sketch, "E57.0.2", {"start": v(-38.1, 0) * mm, "end": v(-38.1, 20.2) * mm});
            skLineSegment(sketch, "E57.0.3", {"start": v(-38.1, 20.2) * mm, "end": v(-38.1, 0) * mm});
            skLineSegment(sketch, "E58", {"start": v(25.4, -4.3) * mm, "end": v(25.4, -21.33) * mm, "construction": true});
            skLineSegment(sketch, "E59", {"start": v(25.4, 4.3) * mm, "end": v(25.4, 21.33) * mm, "construction": true});
            skLineSegment(sketch, "E60", {"start": v(-25.4, -4.3) * mm, "end": v(-25.4, -21.33) * mm, "construction": true});
            skLineSegment(sketch, "E61", {"start": v(-25.4, 4.3) * mm, "end": v(-25.4, 21.33) * mm, "construction": true});
            skLineSegment(sketch, "E62", {"start": v(28.57, -21.33) * mm, "end": v(28.57, 21.33) * mm, "construction": true});
            skLineSegment(sketch, "E63", {"start": v(22.23, 21.33) * mm, "end": v(22.23, -21.33) * mm, "construction": true});
            skLineSegment(sketch, "E64", {"start": v(0, -32.03) * mm, "end": v(0, 39.03) * mm, "construction": true});
            skLineSegment(sketch, "E65", {"start": v(28.58, -21.33) * mm, "end": v(25.4, -18.15) * mm});
            skLineSegment(sketch, "E66", {"start": v(25.4, -18.15) * mm, "end": v(22.23, -21.33) * mm});
            skLineSegment(sketch, "E67", {"start": v(38.1, 0) * mm, "end": v(0, 0) * mm, "construction": true});
            skLineSegment(sketch, "E68.MirrorCS", {"start": v(28.57, 21.33) * mm, "end": v(25.4, 18.15) * mm});
            skLineSegment(sketch, "E69.MirrorCS", {"start": v(25.4, 18.15) * mm, "end": v(22.23, 21.33) * mm});
            skLineSegment(sketch, "E70", {"start": v(-22.23, -21.33) * mm, "end": v(-22.23, 21.33) * mm, "construction": true});
            skLineSegment(sketch, "E71", {"start": v(-28.57, -21.33) * mm, "end": v(-28.57, 21.33) * mm, "construction": true});
            skLineSegment(sketch, "E72", {"start": v(-22.23, -21.33) * mm, "end": v(-25.4, -18.15) * mm});
            skLineSegment(sketch, "E73", {"start": v(-25.4, -18.15) * mm, "end": v(-28.57, -21.33) * mm});
            skLineSegment(sketch, "E74", {"start": v(49.11, -18.15) * mm, "end": v(-64.17, -18.15) * mm, "construction": true});
            skLineSegment(sketch, "E75.MirrorCS", {"start": v(-22.23, 21.33) * mm, "end": v(-25.4, 18.15) * mm});
            skLineSegment(sketch, "E76.MirrorCS", {"start": v(-25.4, 18.15) * mm, "end": v(-28.57, 21.33) * mm});
            const initialGuessF9  = {"E54.0.5": [0, -0.020205576272405608, -1, 0, 0.02698750000000002, 0.019083044257271958, 4.222431654130963, 5.202346306638417], "E54.0.14": [0, -0.002245064030267274, -1, 0, 0.02698750000000002, 0.019083044257271958, 1.080839000541168, 2.060753653048624], "E55.0.3": [0, 0.020205576272405615, 1, 0, 0.02698750000000002, 0.01908304425727196, 4.222431654130961, 5.202346306638417], "E55.0.12": [0, 0.00224506403026728, 1, 0, 0.02698750000000002, 0.01908304425727196, 1.0808390005411688, 2.060753653048625]};
            skSetInitialGuess(sketch, initialGuessF9);
            skSolve(sketch);
        }
        {
            var Q0;
            {var subQ2=sQuery(id+"F9.wireOp",EDGE,"E75.MirrorCS");Q0=makeQuery(id+"F9.imprint","IMPRINT",FACE,{"disambiguationData":[TD([[makeQuery(id+"F9.imprint","IMPRINT",EDGE,{"derivedFrom":subQ2}),-1.0]])]});}
            var Q1;
            {var subQ2=sQuery(id+"F9.wireOp",EDGE,"E72");Q1=makeQuery(id+"F9.imprint","IMPRINT",FACE,{"disambiguationData":[TD([[makeQuery(id+"F9.imprint","IMPRINT",EDGE,{"derivedFrom":subQ2}),1.0]])]});}
            var Q2;
            {var subQ2=sQuery(id+"F9.wireOp",EDGE,"E68.MirrorCS");Q2=makeQuery(id+"F9.imprint","IMPRINT",FACE,{"disambiguationData":[TD([[makeQuery(id+"F9.imprint","IMPRINT",EDGE,{"derivedFrom":subQ2}),-1.0]])]});}
            var Q3;
            {var subQ2=sQuery(id+"F9.wireOp",EDGE,"E65");Q3=makeQuery(id+"F9.imprint","IMPRINT",FACE,{"disambiguationData":[TD([[makeQuery(id+"F9.imprint","IMPRINT",EDGE,{"derivedFrom":subQ2}),1.0]])]});}
            extrude(context, id + "F10", {"entities" : qUnion([Q0, Q1, Q2, Q3]), "operationType" : NewBodyOperationType.REMOVE, "endBound" : BoundingType.SYMMETRIC, "oppositeDirection" : true, "depth" : 25.4 * mm, "offsetDistance" : 25.4 * mm});
        }
        {
            var Q0;
            {var subQ0=sQuery(id+"F0.wireOp",EDGE,"E3.right");Q0=makeQuery(id+"F4.boolean.opBoolean","SPLIT",FACE,{"disambiguationData":[TD([makeQuery(id+"F4.opExtrude","SWEPT_FACE",FACE,{"disambiguationData":[OSD([sQuery(id+"F3.wireOp",EDGE,"E15")])]})])],"derivedFrom":makeQuery(id+"F1.opExtrude","SWEPT_FACE",FACE,{"disambiguationData":[OSD([subQ0])]})});}
            var sketch = newSketch(context, id + "F11", { "sketchPlane" : qUnion([Q0])});
            skLineSegment(sketch, "E77.0.0", {"start": v(-28.58, -14.29) * mm, "end": v(-25.4, -9.8) * mm, "construction": true});
            skLineSegment(sketch, "E77.0.1", {"start": v(-25.4, -9.8) * mm, "end": v(-22.23, -14.29) * mm, "construction": true});
            skLineSegment(sketch, "E77.0.2", {"start": v(-22.23, -14.29) * mm, "end": v(-12.7, -14.29) * mm, "construction": true});
            skLineSegment(sketch, "E77.0.3", {"start": v(-12.7, -14.29) * mm, "end": v(-12.7, 14.29) * mm, "construction": true});
            skLineSegment(sketch, "E77.0.4", {"start": v(-12.7, 14.29) * mm, "end": v(-22.23, 14.29) * mm, "construction": true});
            skLineSegment(sketch, "E77.0.5", {"start": v(-22.23, 14.29) * mm, "end": v(-25.4, 9.8) * mm, "construction": true});
            skLineSegment(sketch, "E77.0.6", {"start": v(-25.4, 9.8) * mm, "end": v(-28.58, 14.29) * mm, "construction": true});
            skLineSegment(sketch, "E77.0.7", {"start": v(-28.57, 14.29) * mm, "end": v(-36.51, 14.29) * mm, "construction": true});
            skLineSegment(sketch, "E77.0.8", {"start": v(-36.51, 14.29) * mm, "end": v(-36.51, -14.29) * mm, "construction": true});
            skLineSegment(sketch, "E77.0.9", {"start": v(-36.51, -14.29) * mm, "end": v(-28.58, -14.29) * mm, "construction": true});
            skLineSegment(sketch, "E78.0.0", {"start": v(25.4, -9.8) * mm, "end": v(28.57, -14.29) * mm, "construction": true});
            skLineSegment(sketch, "E78.0.1", {"start": v(28.57, -14.29) * mm, "end": v(36.51, -14.29) * mm, "construction": true});
            skLineSegment(sketch, "E78.0.2", {"start": v(36.51, -14.29) * mm, "end": v(36.51, 14.29) * mm, "construction": true});
            skLineSegment(sketch, "E78.0.3", {"start": v(36.51, 14.29) * mm, "end": v(28.58, 14.29) * mm, "construction": true});
            skLineSegment(sketch, "E78.0.4", {"start": v(28.58, 14.29) * mm, "end": v(25.4, 9.8) * mm, "construction": true});
            skLineSegment(sketch, "E78.0.5", {"start": v(25.4, 9.8) * mm, "end": v(22.23, 14.29) * mm, "construction": true});
            skLineSegment(sketch, "E78.0.6", {"start": v(22.23, 14.29) * mm, "end": v(12.7, 14.29) * mm, "construction": true});
            skLineSegment(sketch, "E78.0.7", {"start": v(12.7, 14.29) * mm, "end": v(12.7, -14.29) * mm, "construction": true});
            skLineSegment(sketch, "E78.0.8", {"start": v(12.7, -14.29) * mm, "end": v(22.23, -14.29) * mm, "construction": true});
            skLineSegment(sketch, "E78.0.9", {"start": v(22.23, -14.29) * mm, "end": v(25.4, -9.8) * mm, "construction": true});
            skLineSegment(sketch, "E79", {"start": v(-25.4, 9.8) * mm, "end": v(-25.4, -9.8) * mm, "construction": true});
            skLineSegment(sketch, "E80", {"start": v(-36.51, 0) * mm, "end": v(-12.7, 0) * mm, "construction": true});
            skLineSegment(sketch, "E81", {"start": v(-25.4, 4.5) * mm, "end": v(-29.9, 0) * mm});
            skLineSegment(sketch, "E82", {"start": v(-29.9, 0) * mm, "end": v(-25.4, -4.5) * mm});
            skLineSegment(sketch, "E83", {"start": v(-25.4, -4.5) * mm, "end": v(-20.9, 0) * mm});
            skLineSegment(sketch, "E84", {"start": v(-20.9, 0) * mm, "end": v(-25.4, 4.5) * mm});
            skSolve(sketch);
        }
        {
            var Q0;
            Q0=qCreatedBy(makeId("Top.planeOp"),FACE);
            var sketch = newSketch(context, id + "F12", { "sketchPlane" : qUnion([Q0])});
            skPoint(sketch, "E85.0", {"position": v(-15.87, 29.9) * mm});
            skLineSegment(sketch, "E86", {"start": v(-15.87, 29.9) * mm, "end": v(-15.08, 29.9) * mm, "construction": true});
            skLineSegment(sketch, "E87.0", {"start": v(-15.87, 28.57) * mm, "end": v(-15.87, 36.51) * mm, "construction": true});
            skLineSegment(sketch, "E88", {"start": v(-15.08, 29.9) * mm, "end": v(-15.87, 30.35) * mm});
            skLineSegment(sketch, "E89", {"start": v(-15.08, 29.9) * mm, "end": v(-15.87, 29.43) * mm});
            skLineSegment(sketch, "E90", {"start": v(-15.87, 30.35) * mm, "end": v(-15.87, 29.43) * mm});
            skSolve(sketch);
        }
        {
            var Q0;
            Q0 = qSketchRegion(id + "F12", true);
            var Q1;
            Q1 = qConstructionFilter(qBodyType(qCreatedBy(id + "F11" ,EDGE), BodyType.WIRE), ConstructionObject.NO);
            sweep(context, id + "F13", {"operationType" : NewBodyOperationType.REMOVE, "profiles" : qUnion([Q0]), "path" : qUnion([Q1])});
        }
    });
